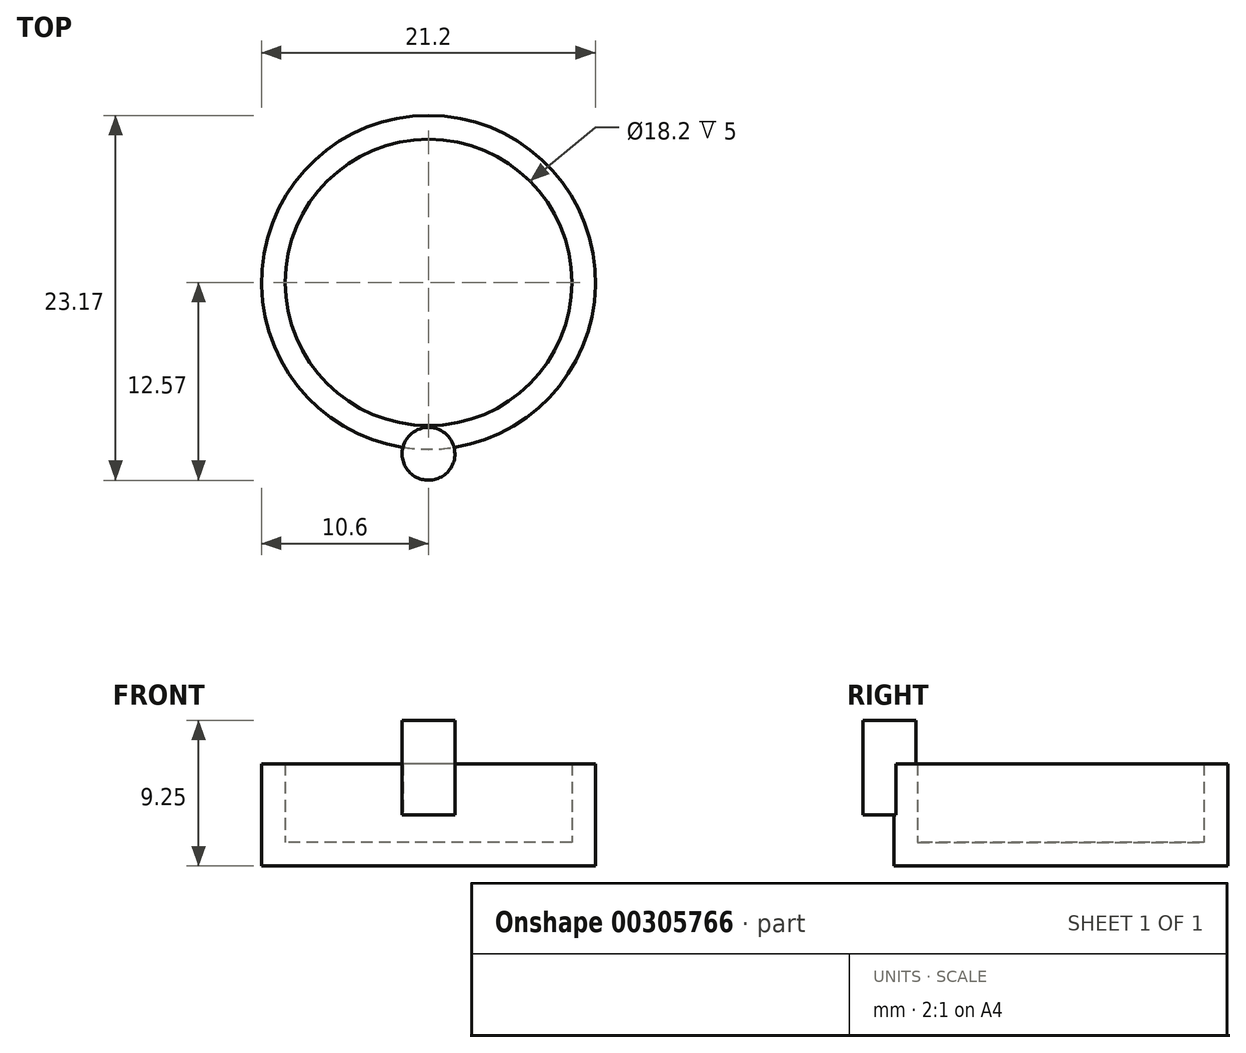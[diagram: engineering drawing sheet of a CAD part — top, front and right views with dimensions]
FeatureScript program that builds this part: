
annotation { "Feature Type Name" : "Feature", "Feature Type Description" : "" }
export const myFeature = defineFeature(function(context is Context, id is Id, definition is map)
    precondition{}
    {
        {
            var Q0;
            Q0=qCreatedBy(makeId("Top.planeOp"),FACE);
            var sketch = newSketch(context, id + "F0", { "sketchPlane" : qUnion([Q0])});
            skCircle(sketch, "E0", {"center": v(0, 0) * mm, "radius": 10.6 * mm});
            skSolve(sketch);
        }
        {
            var Q0;
            Q0 = qSketchRegion(id + "F0", true);
            extrude(context, id + "F1", {"entities" : qUnion([Q0]), "endBound" : BoundingType.SYMMETRIC, "depth" : 6.5 * mm});
        }
        {
            var Q0;
            Q0=makeQuery(id+"F1.opExtrude","CAP_FACE",FACE,{"disambiguationData":[OSD([sQuery(id+"F0.wireOp",EDGE,"E0")])],"isStart":false});
            shell(context, id + "F2", {"entities" : qUnion([Q0]), "thickness" : 1.5 * mm});
        }
        {
            var Q0;
            Q0=qCreatedBy(makeId("Top.planeOp"),FACE);
            var sketch = newSketch(context, id + "F3", { "sketchPlane" : qUnion([Q0])});
            skCircle(sketch, "E1", {"center": v(0, -10.9) * mm, "radius": 1.68 * mm});
            skSolve(sketch);
        }
        {
            var Q0;
            Q0 = qSketchRegion(id + "F3", true);
            extrude(context, id + "F4", {"entities" : qUnion([Q0]), "operationType" : NewBodyOperationType.ADD, "depth" : 6 * mm});
        }
    });
